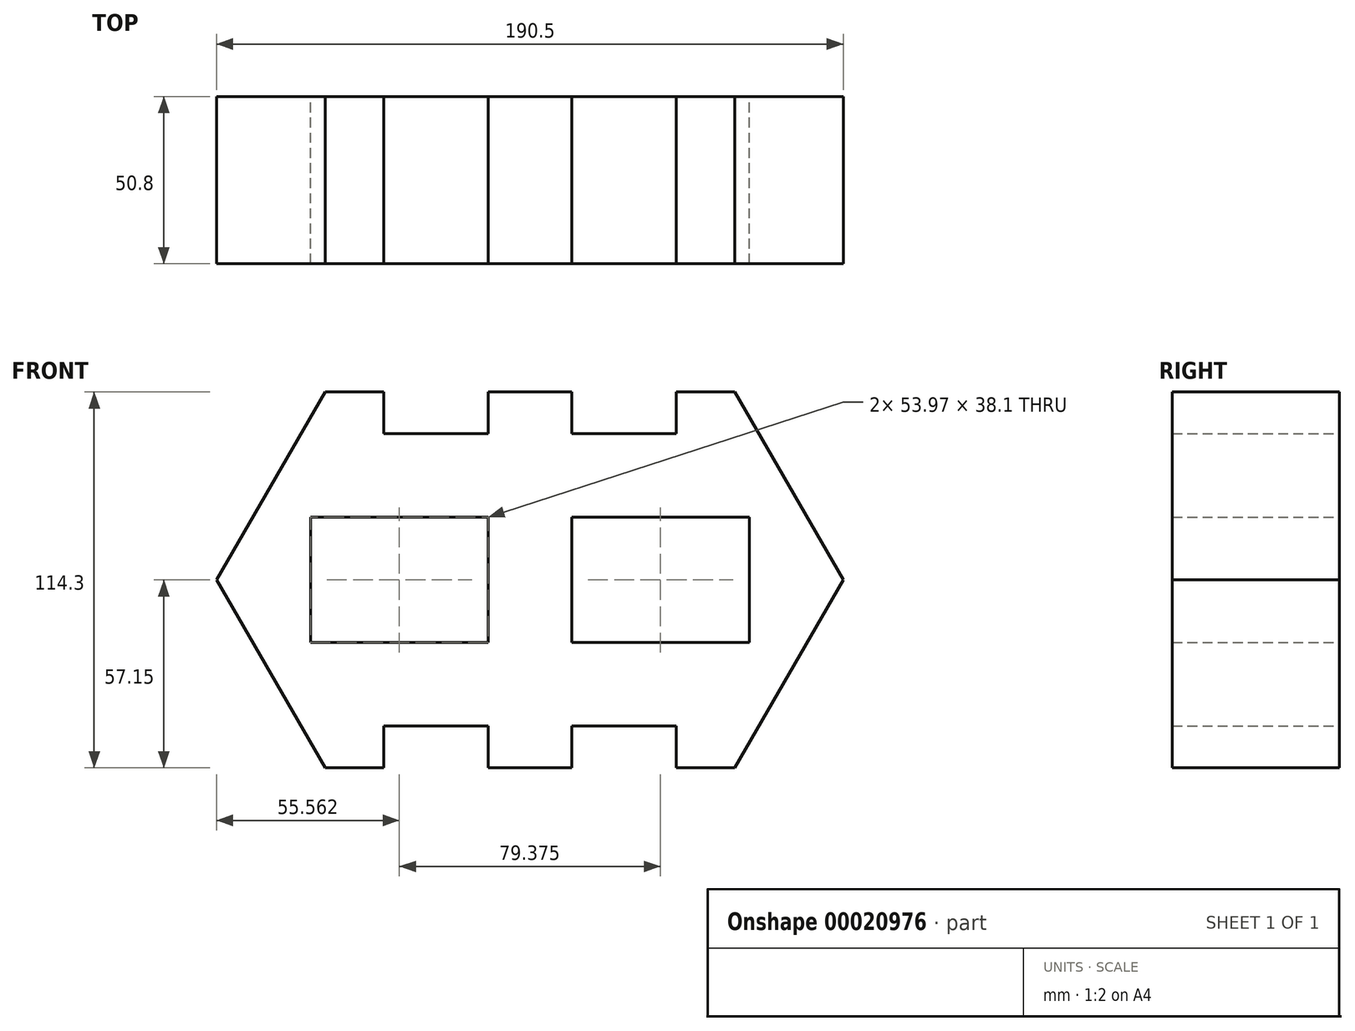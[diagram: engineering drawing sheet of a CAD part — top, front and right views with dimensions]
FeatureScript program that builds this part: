
annotation { "Feature Type Name" : "Feature", "Feature Type Description" : "" }
export const myFeature = defineFeature(function(context is Context, id is Id, definition is map)
    precondition{}
    {
        {
            var Q0;
            Q0=qCreatedBy(makeId("Front.planeOp"),FACE);
            var sketch = newSketch(context, id + "F0", { "sketchPlane" : qUnion([Q0])});
            skLineSegment(sketch, "E0", {"start": v(0, 0) * mm, "end": v(95.25, 0) * mm});
            skLineSegment(sketch, "E1", {"start": v(62.25, 57.15) * mm, "end": v(44.45, 57.15) * mm});
            skLineSegment(sketch, "E2", {"start": v(0, 57.15) * mm, "end": v(0, 0) * mm});
            skLineSegment(sketch, "E3", {"start": v(12.7, 57.15) * mm, "end": v(12.7, 44.45) * mm});
            skLineSegment(sketch, "E4.trimOffspring", {"start": v(12.7, 57.15) * mm, "end": v(0, 57.15) * mm});
            skLineSegment(sketch, "E5", {"start": v(12.7, 44.45) * mm, "end": v(44.45, 44.45) * mm});
            skLineSegment(sketch, "E6", {"start": v(44.45, 44.45) * mm, "end": v(44.45, 57.15) * mm});
            skPoint(sketch, "E7.end.orphan", {"position": v(69.85, 57.15) * mm});
            skLineSegment(sketch, "E8", {"start": v(95.25, 0) * mm, "end": v(62.25, 57.15) * mm});
            skPoint(sketch, "E9.end.orphan", {"position": v(95.25, 57.15) * mm});
            skLineSegment(sketch, "E10.MirrorCS", {"start": v(0, -57.15) * mm, "end": v(0, 0) * mm});
            skLineSegment(sketch, "E11.MirrorCS", {"start": v(12.7, -57.15) * mm, "end": v(0, -57.15) * mm});
            skLineSegment(sketch, "E12.MirrorCS", {"start": v(12.7, -57.15) * mm, "end": v(12.7, -44.45) * mm});
            skLineSegment(sketch, "E13.MirrorCS", {"start": v(12.7, -44.45) * mm, "end": v(44.45, -44.45) * mm});
            skLineSegment(sketch, "E14.MirrorCS", {"start": v(44.45, -44.45) * mm, "end": v(44.45, -57.15) * mm});
            skLineSegment(sketch, "E15.MirrorCS", {"start": v(62.25, -57.15) * mm, "end": v(44.45, -57.15) * mm});
            skLineSegment(sketch, "E16.MirrorCS", {"start": v(95.25, 0) * mm, "end": v(62.25, -57.15) * mm});
            skPoint(sketch, "E17", {"position": v(95.25, -57.15) * mm});
            skLineSegment(sketch, "E18", {"start": v(95.25, 57.15) * mm, "end": v(95.25, -57.15) * mm});
            skPoint(sketch, "E19", {"position": v(95.25, 0) * mm});
            skLineSegment(sketch, "E20", {"start": v(95.25, 0) * mm, "end": v(95.25, -57.15) * mm});
            skLineSegment(sketch, "E21", {"start": v(0, 0) * mm, "end": v(12.7, 0) * mm});
            skLineSegment(sketch, "E22", {"start": v(12.7, -19.05) * mm, "end": v(12.7, 0) * mm});
            skLineSegment(sketch, "E23", {"start": v(12.7, -19.05) * mm, "end": v(66.67, -19.05) * mm});
            skLineSegment(sketch, "E24", {"start": v(66.67, 0) * mm, "end": v(66.67, -19.05) * mm});
            skLineSegment(sketch, "E25.MirrorCS", {"start": v(12.7, 19.05) * mm, "end": v(12.7, 0) * mm});
            skLineSegment(sketch, "E26.MirrorCS", {"start": v(12.7, 19.05) * mm, "end": v(66.67, 19.05) * mm});
            skLineSegment(sketch, "E27.MirrorCS", {"start": v(66.67, 0) * mm, "end": v(66.67, 19.05) * mm});
            skLineSegment(sketch, "E28.MirrorCS", {"start": v(-12.7, 57.15) * mm, "end": v(0, 57.15) * mm});
            skLineSegment(sketch, "E29.MirrorCS", {"start": v(-12.7, 57.15) * mm, "end": v(-12.7, 44.45) * mm});
            skLineSegment(sketch, "E30.MirrorCS", {"start": v(-12.7, 44.45) * mm, "end": v(-44.45, 44.45) * mm});
            skLineSegment(sketch, "E31.MirrorCS", {"start": v(-44.45, 44.45) * mm, "end": v(-44.45, 57.15) * mm});
            skLineSegment(sketch, "E32.MirrorCS", {"start": v(-62.25, 57.15) * mm, "end": v(-44.45, 57.15) * mm});
            skLineSegment(sketch, "E33.MirrorCS", {"start": v(-95.25, 0) * mm, "end": v(-62.25, 57.15) * mm});
            skLineSegment(sketch, "E34.MirrorCS", {"start": v(0, 0) * mm, "end": v(-95.25, 0) * mm});
            skLineSegment(sketch, "E35.MirrorCS", {"start": v(-12.7, -19.05) * mm, "end": v(-12.7, 0) * mm});
            skLineSegment(sketch, "E36.MirrorCS", {"start": v(-12.7, -19.05) * mm, "end": v(-66.67, -19.05) * mm});
            skLineSegment(sketch, "E37.MirrorCS", {"start": v(-66.67, 0) * mm, "end": v(-66.67, -19.05) * mm});
            skLineSegment(sketch, "E38.MirrorCS", {"start": v(-66.67, 19.05) * mm, "end": v(-66.67, 0) * mm});
            skLineSegment(sketch, "E39.MirrorCS", {"start": v(-12.7, 19.05) * mm, "end": v(-12.7, 0) * mm});
            skLineSegment(sketch, "E40.MirrorCS", {"start": v(-12.7, 19.05) * mm, "end": v(-66.67, 19.05) * mm});
            skLineSegment(sketch, "E41.MirrorCS", {"start": v(-12.7, -57.15) * mm, "end": v(0, -57.15) * mm});
            skLineSegment(sketch, "E42.MirrorCS", {"start": v(-12.7, -57.15) * mm, "end": v(-12.7, -44.45) * mm});
            skLineSegment(sketch, "E43.MirrorCS", {"start": v(-44.45, -44.45) * mm, "end": v(-44.45, -57.15) * mm});
            skLineSegment(sketch, "E44.MirrorCS", {"start": v(-12.7, -44.45) * mm, "end": v(-44.45, -44.45) * mm});
            skLineSegment(sketch, "E45.MirrorCS", {"start": v(-62.25, -57.15) * mm, "end": v(-44.45, -57.15) * mm});
            skLineSegment(sketch, "E46.MirrorCS", {"start": v(-95.25, 0) * mm, "end": v(-62.25, -57.15) * mm});
            skSolve(sketch);
        }
        {
            var Q0;
            Q0 = qSketchRegion(id + "F0", true);
            extrude(context, id + "F1", {"entities" : qUnion([Q0]), "depth" : 50.8 * mm});
        }
    });
